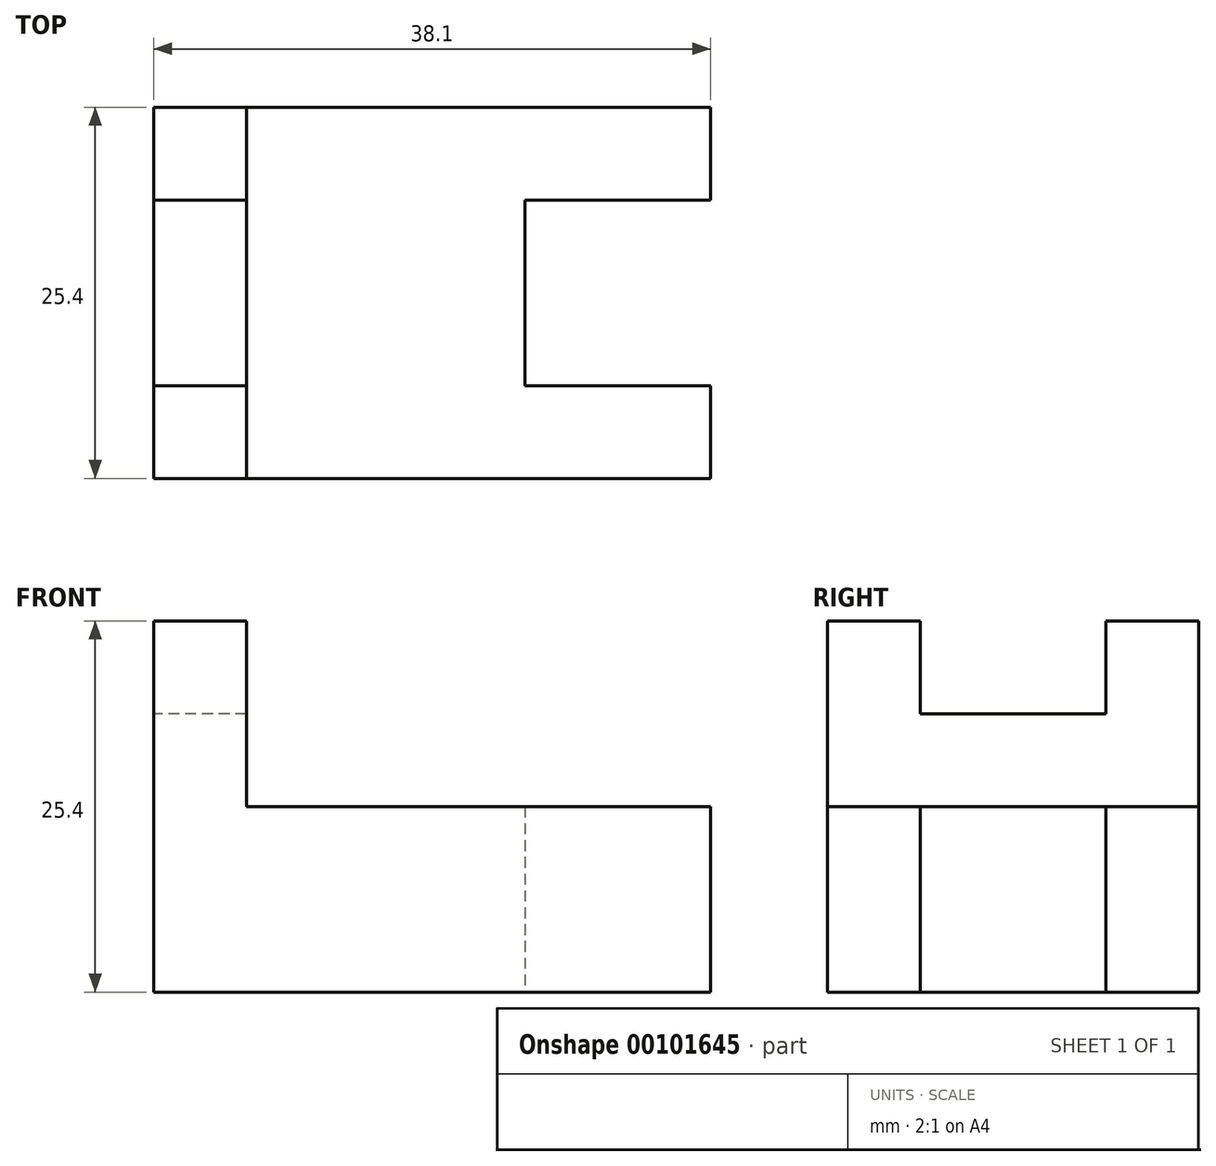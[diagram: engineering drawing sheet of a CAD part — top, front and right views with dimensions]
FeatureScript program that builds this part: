
annotation { "Feature Type Name" : "Feature", "Feature Type Description" : "" }
export const myFeature = defineFeature(function(context is Context, id is Id, definition is map)
    precondition{}
    {
        {
            var Q0;
            Q0=qCreatedBy(makeId("Front.planeOp"),FACE);
            var sketch = newSketch(context, id + "F0", { "sketchPlane" : qUnion([Q0])});
            skLineSegment(sketch, "E0", {"start": v(0, 0) * mm, "end": v(38.1, 0) * mm});
            skLineSegment(sketch, "E1", {"start": v(38.1, 0) * mm, "end": v(38.1, 12.7) * mm});
            skLineSegment(sketch, "E2", {"start": v(38.1, 12.7) * mm, "end": v(6.35, 12.7) * mm});
            skLineSegment(sketch, "E3", {"start": v(6.35, 12.7) * mm, "end": v(6.35, 25.4) * mm});
            skLineSegment(sketch, "E4", {"start": v(6.35, 25.4) * mm, "end": v(0, 25.4) * mm});
            skLineSegment(sketch, "E5", {"start": v(0, 25.4) * mm, "end": v(0, 0) * mm});
            skLineSegment(sketch, "E6", {"start": v(6.35, 19.05) * mm, "end": v(0, 19.05) * mm});
            skLineSegment(sketch, "E7", {"start": v(25.4, 12.7) * mm, "end": v(25.4, 0) * mm});
            skSolve(sketch);
        }
        {
            var Q0;
            Q0 = qSketchRegion(id + "F0", true);
            extrude(context, id + "F1", {"entities" : qUnion([Q0]), "endBound" : BoundingType.SYMMETRIC, "depth" : 25.4 * mm});
        }
        {
            var Q0;
            {var subQ0=sQuery(id+"F0.wireOp",EDGE,"E4");Q0=makeQuery(id+"F0.imprint","IMPRINT",FACE,{"disambiguationData":[TD([[makeQuery(id+"F0.imprint","IMPRINT",EDGE,{"derivedFrom":subQ0}),1.0]])]});}
            var Q1;
            {var subQ0=sQuery(id+"F0.wireOp",EDGE,"E1");Q1=makeQuery(id+"F0.imprint","IMPRINT",FACE,{"disambiguationData":[TD([[makeQuery(id+"F0.imprint","IMPRINT",EDGE,{"derivedFrom":subQ0}),1.0]])]});}
            extrude(context, id + "F2", {"entities" : qUnion([Q0, Q1]), "operationType" : NewBodyOperationType.REMOVE, "endBound" : BoundingType.SYMMETRIC, "oppositeDirection" : true, "depth" : 12.7 * mm});
        }
    });
